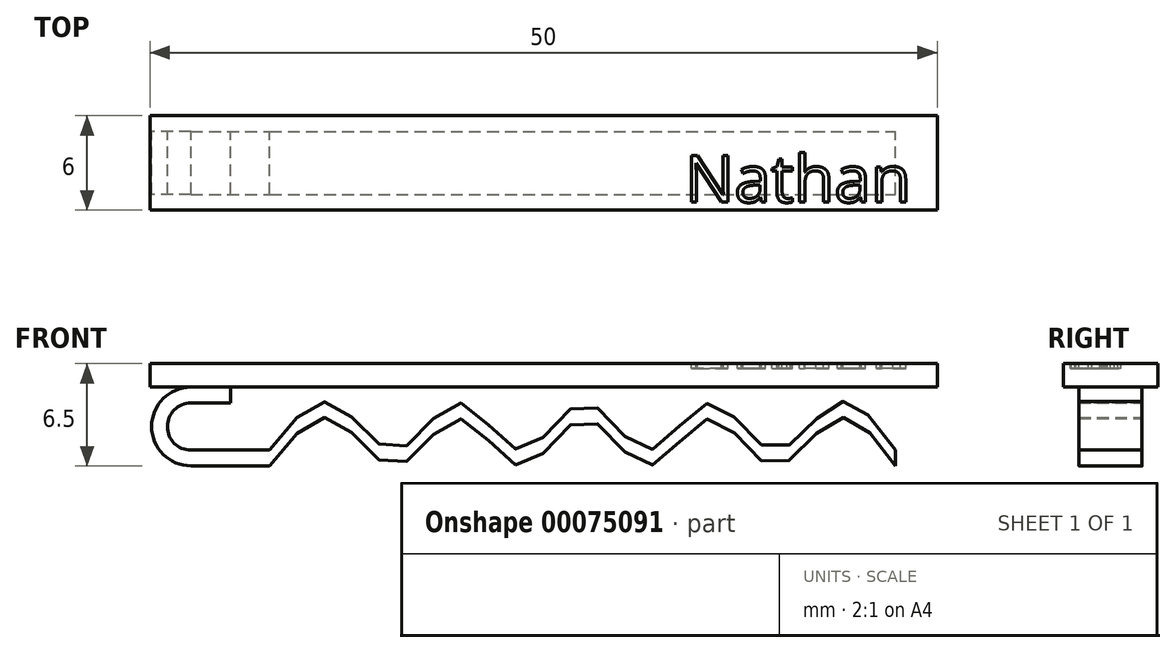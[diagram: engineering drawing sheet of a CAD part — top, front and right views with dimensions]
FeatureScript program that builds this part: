
annotation { "Feature Type Name" : "Feature", "Feature Type Description" : "" }
export const myFeature = defineFeature(function(context is Context, id is Id, definition is map)
    precondition{}
    {
        {
            var Q0;
            Q0=qCreatedBy(makeId("Top.planeOp"),FACE);
            var sketch = newSketch(context, id + "F0", { "sketchPlane" : qUnion([Q0])});
            skLineSegment(sketch, "E0.bottom", {"start": v(-24.27, 3) * mm, "end": v(25.73, 3) * mm});
            skLineSegment(sketch, "E0.top", {"start": v(-24.27, -3) * mm, "end": v(25.73, -3) * mm});
            skLineSegment(sketch, "E0.left", {"start": v(-24.27, 3) * mm, "end": v(-24.27, -3) * mm});
            skLineSegment(sketch, "E0.right", {"start": v(25.73, 3) * mm, "end": v(25.73, -3) * mm});
            skSolve(sketch);
        }
        {
            var Q0;
            Q0=makeQuery(id+"F0.imprint","IMPRINT",FACE,{"disambiguationData":[TD([[makeQuery(id+"F0.imprint","IMPRINT",EDGE,{"derivedFrom":sQuery(id+"F0.wireOp",EDGE,"E0.bottom")}),-1.0]])]});
            extrude(context, id + "F1", {"entities" : qUnion([Q0]), "depth" : 1.5 * mm});
        }
        {
            var Q0;
            Q0=qCreatedBy(makeId("Front.planeOp"),FACE);
            var sketch = newSketch(context, id + "F2", { "sketchPlane" : qUnion([Q0])});
            skCircle(sketch, "E1", {"center": v(-21.67, -2.5) * mm, "radius": 2.5 * mm});
            skLineSegment(sketch, "E2", {"start": v(-24.23, 0) * mm, "end": v(-24.23, -5) * mm, "construction": true});
            skLineSegment(sketch, "E3", {"start": v(-21.67, -2.5) * mm, "end": v(-19.17, -2.5) * mm, "construction": true});
            skLineSegment(sketch, "E4", {"start": v(-19.17, -2.5) * mm, "end": v(-19.17, 0) * mm, "construction": true});
            skLineSegment(sketch, "E5.bottom", {"start": v(-21.67, 0) * mm, "end": v(-19.17, 0) * mm});
            skLineSegment(sketch, "E5.top", {"start": v(-21.67, -1) * mm, "end": v(-19.17, -1) * mm});
            skLineSegment(sketch, "E5.left", {"start": v(-21.67, 0) * mm, "end": v(-21.67, -1) * mm});
            skLineSegment(sketch, "E5.right", {"start": v(-19.17, 0) * mm, "end": v(-19.17, -1) * mm});
            skCircle(sketch, "E6", {"center": v(-21.67, -2.5) * mm, "radius": 1.5 * mm});
            skLineSegment(sketch, "E7", {"start": v(-21.67, -2.5) * mm, "end": v(-21.67, -5) * mm, "construction": true});
            skLineSegment(sketch, "E8.bottom", {"start": v(-21.67, -5) * mm, "end": v(-16.67, -5) * mm});
            skLineSegment(sketch, "E8.top", {"start": v(-21.67, -4) * mm, "end": v(-16.67, -4) * mm});
            skLineSegment(sketch, "E8.left", {"start": v(-21.67, -5) * mm, "end": v(-21.67, -4) * mm});
            skLineSegment(sketch, "E8.right", {"start": v(-16.67, -5) * mm, "end": v(-16.67, -4) * mm});
            skLineSegment(sketch, "E9", {"start": v(-24.23, -5) * mm, "end": v(26.09, -5) * mm, "construction": true});
            skLineSegment(sketch, "E10", {"start": v(-21.67, -4) * mm, "end": v(26.09, -4) * mm, "construction": true});
            skPoint(sketch, "E10.endSnap0", {"position": v(-19.17, -4) * mm});
            skLineSegment(sketch, "E11", {"start": v(-19.17, -1) * mm, "end": v(26.09, -1) * mm, "construction": true});
            skLineSegment(sketch, "E12", {"start": v(26.09, 0) * mm, "end": v(26.09, -9.04) * mm, "construction": true});
            skLineSegment(sketch, "E13", {"start": v(23.09, 1.55) * mm, "end": v(23.09, -9.1) * mm, "construction": true});
            skLineSegment(sketch, "E14", {"start": v(-12.67, 0) * mm, "end": v(-12.67, -18.2) * mm, "construction": true});
            skLineSegment(sketch, "E15", {"start": v(-8.67, 0) * mm, "end": v(-8.67, -17.85) * mm, "construction": true});
            skLineSegment(sketch, "E16", {"start": v(-4.67, 0) * mm, "end": v(-4.67, -18.25) * mm, "construction": true});
            skLineSegment(sketch, "E17", {"start": v(-0.67, 0) * mm, "end": v(-0.67, -18.3) * mm, "construction": true});
            skLineSegment(sketch, "E18", {"start": v(-0.67, -18.3) * mm, "end": v(-0.38, -18.3) * mm, "construction": true});
            skLineSegment(sketch, "E19", {"start": v(3.33, 0) * mm, "end": v(3.33, -18.6) * mm, "construction": true});
            skLineSegment(sketch, "E20", {"start": v(3.33, -18.6) * mm, "end": v(3.62, -18.6) * mm, "construction": true});
            skLineSegment(sketch, "E21", {"start": v(7.33, 0) * mm, "end": v(7.33, -18.25) * mm, "construction": true});
            skLineSegment(sketch, "E22", {"start": v(11.33, 0) * mm, "end": v(11.33, -18.36) * mm, "construction": true});
            skLineSegment(sketch, "E23", {"start": v(15.33, 0.13) * mm, "end": v(15.33, -18.46) * mm, "construction": true});
            skLineSegment(sketch, "E24", {"start": v(19.33, 0.13) * mm, "end": v(19.33, -18.12) * mm, "construction": true});
            skFitSpline(sketch, "E25", {"points": [v(-16.67, -4) * mm, v(-12.67, -1) * mm, v(-8.67, -4) * mm, v(-4.67, -1) * mm, v(-0.67, -4) * mm, v(3.33, -1) * mm, v(7.33, -4) * mm, v(11.33, -1) * mm, v(15.33, -4) * mm, v(19.33, -1) * mm, v(23.09, -4) * mm], "startDerivative": vector(39.92, 51.66) * mm, "endDerivative": vector(43.86, -61.06) * mm});
            skLineSegment(sketch, "E26", {"start": v(-19.22, -2) * mm, "end": v(26.09, -2) * mm, "construction": true});
            skFitSpline(sketch, "E27", {"points": [v(-16.67, -5) * mm, v(-12.67, -2) * mm, v(-8.67, -5) * mm, v(-4.67, -2) * mm, v(-0.67, -5) * mm, v(3.33, -2) * mm, v(7.33, -5) * mm, v(11.33, -2) * mm, v(15.33, -5) * mm, v(19.33, -2) * mm, v(23.09, -5) * mm], "startDerivative": vector(39.92, 51.86) * mm, "endDerivative": vector(37.8, -52.4) * mm});
            skLineSegment(sketch, "E28", {"start": v(23.09, -4) * mm, "end": v(23.09, -5) * mm});
            skSolve(sketch);
        }
        {
            var Q0;
            {var subQ0=sQuery(id+"F2.wireOp",EDGE,"E5.left");Q0=makeQuery(id+"F2.imprint","IMPRINT",FACE,{"disambiguationData":[TD([[makeQuery(id+"F2.imprint","IMPRINT",EDGE,{"derivedFrom":subQ0}),-1.0]])]});}
            var Q1;
            {var subQ0=sQuery(id+"F2.wireOp",EDGE,"E5.bottom");Q1=makeQuery(id+"F2.imprint","IMPRINT",FACE,{"disambiguationData":[TD([[makeQuery(id+"F2.imprint","IMPRINT",EDGE,{"derivedFrom":subQ0}),-1.0]])]});}
            var Q2;
            {var subQ0=sQuery(id+"F2.wireOp",EDGE,"E5.left");Q2=makeQuery(id+"F2.imprint","IMPRINT",FACE,{"disambiguationData":[TD([[makeQuery(id+"F2.imprint","IMPRINT",EDGE,{"derivedFrom":subQ0}),1.0]])]});}
            var Q3;
            {var subQ0=sQuery(id+"F2.wireOp",EDGE,"E8.left");Q3=makeQuery(id+"F2.imprint","IMPRINT",FACE,{"disambiguationData":[TD([[makeQuery(id+"F2.imprint","IMPRINT",EDGE,{"derivedFrom":subQ0}),-1.0]])]});}
            var Q4;
            {var subQ0=sQuery(id+"F2.wireOp",EDGE,"E8.bottom");Q4=makeQuery(id+"F2.imprint","IMPRINT",FACE,{"disambiguationData":[TD([[makeQuery(id+"F2.imprint","IMPRINT",EDGE,{"derivedFrom":subQ0}),1.0]])]});}
            var Q5;
            Q5=makeQuery(id+"F2.imprint","IMPRINT",FACE,{"disambiguationData":[TD([[makeQuery(id+"F2.imprint","IMPRINT",EDGE,{"derivedFrom":sQuery(id+"F2.wireOp",EDGE,"E8.right")}),-1.0]])]});
            extrude(context, id + "F3", {"entities" : qUnion([Q0, Q1, Q2, Q3, Q4, Q5]), "operationType" : NewBodyOperationType.ADD, "endBound" : BoundingType.SYMMETRIC, "depth" : 4 * mm});
        }
        {
            var Q0;
            Q0=makeQuery(id+"F1.opExtrude","CAP_FACE",FACE,{"disambiguationData":[OSD([sQuery(id+"F0.wireOp",EDGE,"E0.bottom"),sQuery(id+"F0.wireOp",EDGE,"E0.top"),sQuery(id+"F0.wireOp",EDGE,"E0.left"),sQuery(id+"F0.wireOp",EDGE,"E0.right")])],"isStart":false});
            var sketch = newSketch(context, id + "F4", { "sketchPlane" : qUnion([Q0])});
            skText(sketch, "E29", { "text": "Nathan", "fontName": "OpenSans-Regular.ttf"});
            const initialGuessF4  = {"E29": [0.0097, -0.0025, 1, 0, 0.003]};
            skSetInitialGuess(sketch, initialGuessF4);
            skSolve(sketch);
        }
        {
            var Q0;
            Q0 = qSketchRegion(id + "F4", true);
            extrude(context, id + "F5", {"entities" : qUnion([Q0]), "operationType" : NewBodyOperationType.REMOVE, "oppositeDirection" : true, "depth" : .3 * mm});
        }
    });
